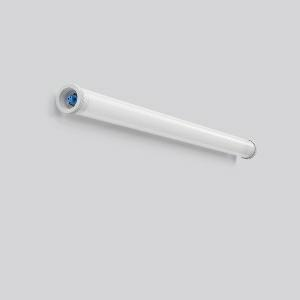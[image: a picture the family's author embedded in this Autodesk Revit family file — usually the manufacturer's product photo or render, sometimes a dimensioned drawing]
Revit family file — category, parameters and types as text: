
# Revit family: planox_tube_601071_002_1_730hf_5701
name_source: partatom
category: Lighting Fixtures
units: mm (PartAtom-declared; Revit-internal decimal feet)

## family parameters
Cut with Voids When Loaded = No
Host = Face
Light Source = No
Part Type = Normal
Room Calculation Point = No
Round Connector Dimension = Use Diameter
Shared = No

## types (1)
- PLANOX TUBE (1 x LED Modul 840, 5350 lm, 4000)
    Apparent Load = 39 VA
    CIE Flux Codes = 42 71 89 90 100
    Color Rendering = 80
    Color Temperature = 4000
    Default Elevation = 1800 mm
    Description = Series: PLANOX TUBE
Robust protective tube luminaire for tough requirements. Rack made of sheet steel, white powder coated. End caps made of plastic (polyamide) grey. Diffuser made of plastic (polycarbonate), opal, shockproof. Symmetrical light distribution. Homogeneous light distribution. With accessories for wall, ceiling or pendant mounting. Suitable for through-wiring. With integrated HF movement sensor. Movement sensor functional parameters: Hold time: can be set with Casambi app. Range: up to 6 m, adjustable in 4 steps. Brightness sensor: adjustable in 5 steps. Factory setting: hold time adjustable via Casambi app, brightness threshold deactivated, detection range 100%. Mounting set must be ordered separately. Luminaire with limited surface temperature in accordance with EN 60598-2-24 for use in environments in which a deposit of conductive dust on the luminaire can be expected. Qualified for use in the food and drink industry. Suitable for lighting in public car parks and public off-street parking spaces according to DIN 67528. Environmentally friendly and resource-saving due to replaceable components. 
Colour: white
Diameter: 78 mm
Length: 1349 mm
Lamp: LED
Socket: without socket
Colour temperature: 4000K
Colour rendering index (CRI): 83
System power: 39 W
Rated luminous flux: 5350 lm
Luminous efficiency: 137 lm/W
Control gear: Dimmable Bluetooth converter
Protection class: I
Type of protection: IP 67
    Height = 0 mm  [stored 0 ft]
    Lamp = 1 x LED Modul 840
    Lamp Light Flux = 5350 lm
    Lamp count = 1
    Length = 1349 mm
    Lifetime = 50000 h
    Luminous efficacy = 137 lm/W
    Manufacturer = RZB
    ModVariant = No
    Model = 601071.002.1.730HF
    Mounting Place = Ceiling, Wall
    Mounting Type = Surface mounted
    Number of Poles = 1
    OnlyDefault = Yes
    Power Factor = 1
    Product Name = PLANOX TUBE
    Product group = Surface mounted luminaires for moist/humid enviroments
    ProductGroupID = 308
    Protection Class = Protection class I
    Protection Degree = Degree of protection
    RLX_Detail_Level = 1
    RLX_Emergency_Light_Flux = 0 lm
    RLX_Emergency_Type = 0
    RLX_Emergency_Type_DB = No
    RlxData = <blob elided: 34001 chars, md5=9b58f0d0>
    Socket = socket
    Standby Power = 0 W
    System Light Flux = 5350 lm
    System Power = 39 W
    Type Comments = Product without accessories
    Type Image = 601071.002.jpg
    URL = http://relux.com
    VarID = ---
    Voltage = 230 V
    Voltage Range = 220-240 V
    Weight = 0.00 kg
    Width = 0 mm  [stored 0 ft]

note: [stored X ft] marks values corroborated as IEEE doubles in the binary element streams (Revit-internal decimal feet)

## geometry (parser evidence)
native form markers: Blend x4, Sweep x13
no freeform markers — native parametric forms only
